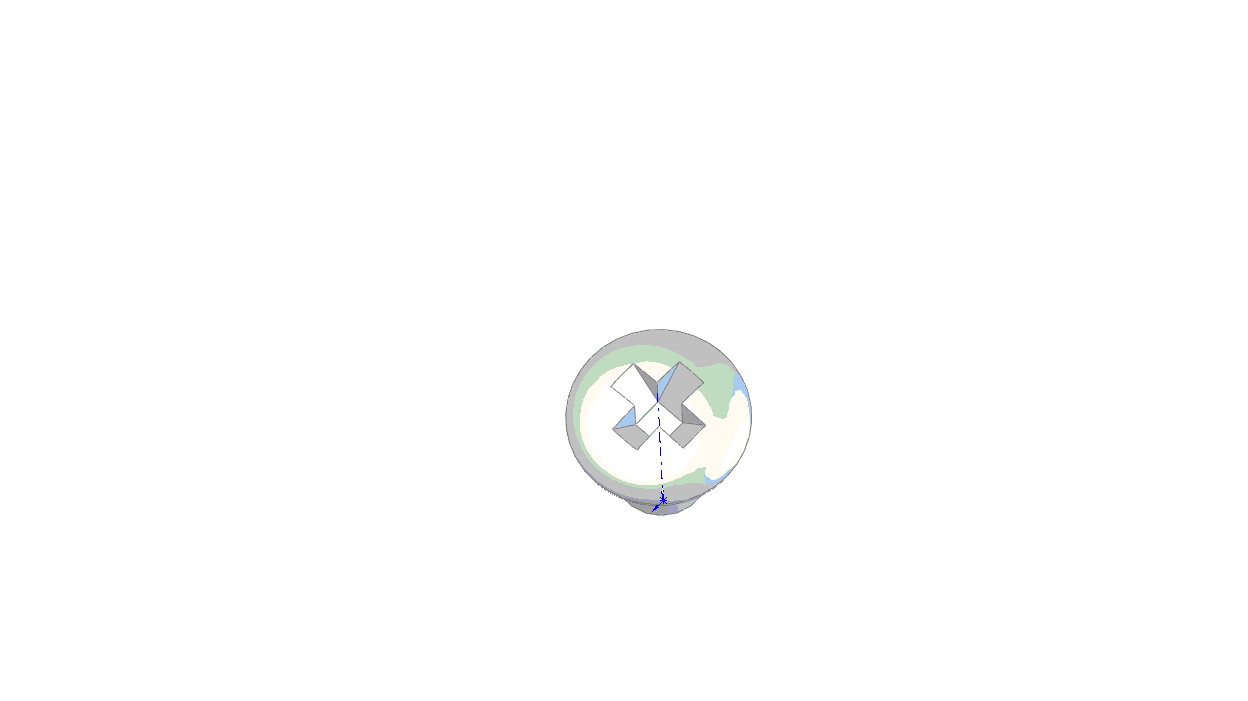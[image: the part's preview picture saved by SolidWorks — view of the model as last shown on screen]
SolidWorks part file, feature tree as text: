
SOLIDWORKS PART (.sldprt)
format: sldprt  version: not decoded by parser v0  size: 134,144 bytes
history: native  units: mm
features: plane x3, sketch x3, material x1, extrude x1, revolve x1, cut_extrude x1, pattern_circular x1, chamfer x1 (+8 scaffold rows collapsed)
feature tree (20):
  scaffold x8  (default folders/planes/origin — collapsed)
  material  "Matériau <non spécifié>"
  plane  "Plan de face"
  plane  "Plan de dessus"
  plane  "Plan de droite"
  sketch  "Esquisse1"  dims[D1=~2.611009mm]
  extrude  "Extrusion1"  Depth=6.4mm
  sketch  "Esquisse2"  dims[D1=0.5mm D2=1.2mm]
  revolve  "Révolution1"  Angle=360deg
  sketch  "Esquisse3"
  cut_extrude  "Enlèv. mat.-Extru.1"  Depth=1mm
  pattern_circular  "Répétition circulaire1"  Count=2 Angle=90deg
  chamfer  "Chanfrein1"  Distance=1.44mm
decode coverage: 7 of 8 modeling features carry decoded parameters
note: ~ marks probable driven/reference dimensions
note: suppression state not decoded; provenance and decode notes live in map.json
